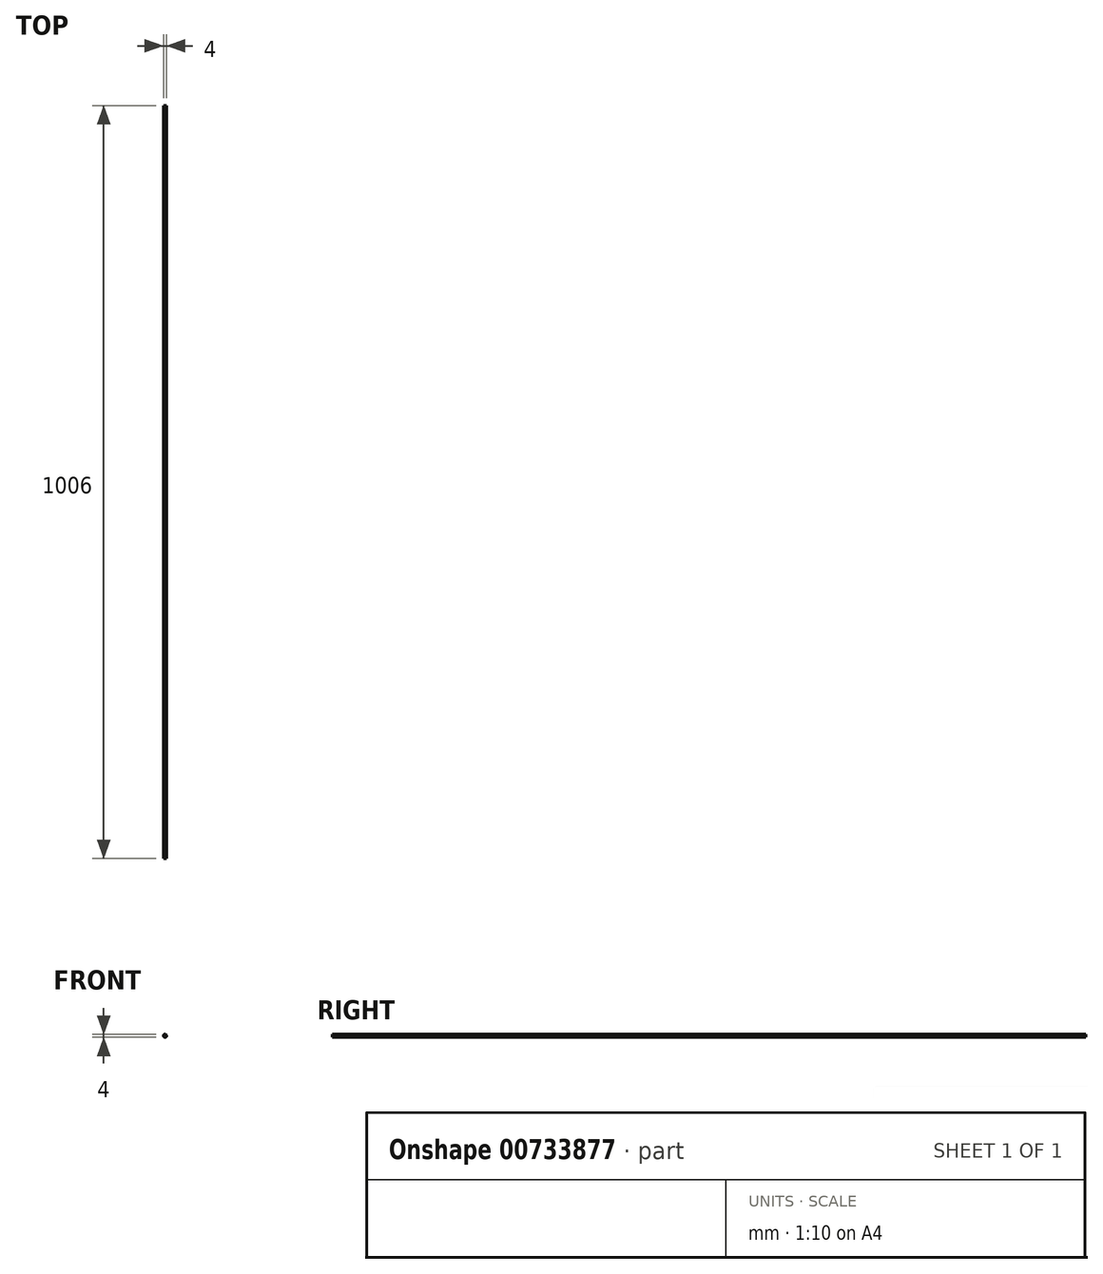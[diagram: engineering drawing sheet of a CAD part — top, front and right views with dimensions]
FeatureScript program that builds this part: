
annotation { "Feature Type Name" : "Feature", "Feature Type Description" : "" }
export const myFeature = defineFeature(function(context is Context, id is Id, definition is map)
    precondition{}
    {
        {
            var Q0;
            Q0=qCreatedBy(makeId("Front.planeOp"),FACE);
            var sketch = newSketch(context, id + "F0", { "sketchPlane" : qUnion([Q0])});
            skCircle(sketch, "E0", {"center": v(0, 0) * mm, "radius": 2 * mm});
            skSolve(sketch);
        }
        {
            var Q0;
            Q0=makeQuery(id+"F0.imprint","IMPRINT",FACE,{"disambiguationData":[TD([[makeQuery(id+"F0.imprint","IMPRINT",EDGE,{"derivedFrom":sQuery(id+"F0.wireOp",EDGE,"E0")}),1.0]])]});
            extrude(context, id + "F1", {"entities" : qUnion([Q0]), "depth" : 1006 * mm, "offsetDistance" : 25 * mm});
        }
    });
